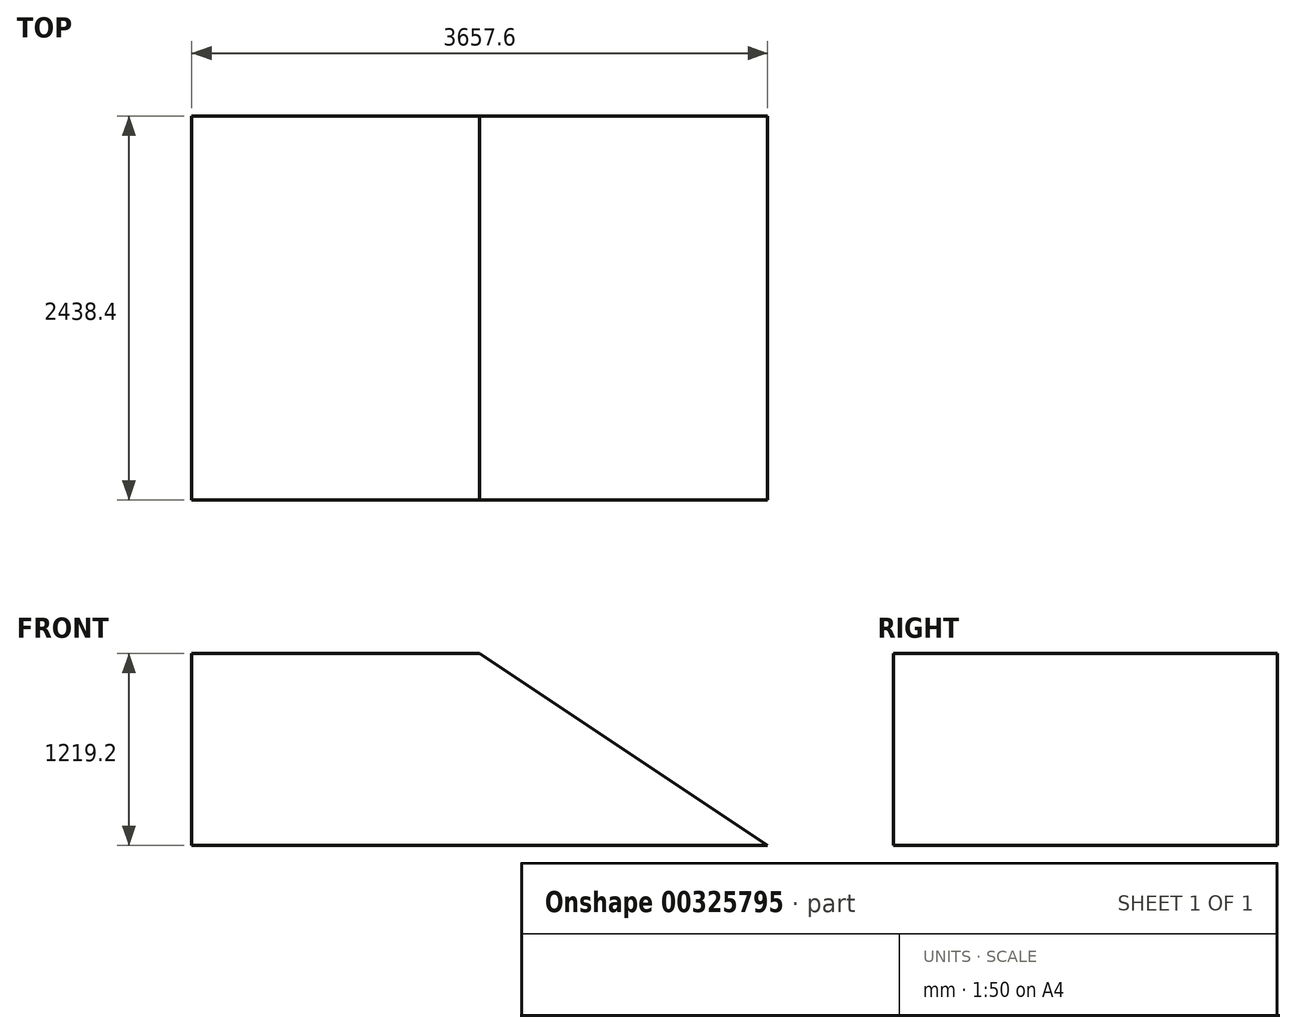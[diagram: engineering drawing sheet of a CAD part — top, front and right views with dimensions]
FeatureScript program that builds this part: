
annotation { "Feature Type Name" : "Feature", "Feature Type Description" : "" }
export const myFeature = defineFeature(function(context is Context, id is Id, definition is map)
    precondition{}
    {
        {
            var Q0;
            Q0=qCreatedBy(makeId("Front.planeOp"),FACE);
            var sketch = newSketch(context, id + "F0", { "sketchPlane" : qUnion([Q0])});
            skLineSegment(sketch, "E0.bottom", {"start": v(0, 0) * mm, "end": v(1828.8, 0) * mm});
            skLineSegment(sketch, "E0.top", {"start": v(0, 1219.2) * mm, "end": v(1828.8, 1219.2) * mm});
            skLineSegment(sketch, "E0.left", {"start": v(0, 0) * mm, "end": v(0, 1219.2) * mm});
            skLineSegment(sketch, "E0.right", {"start": v(1828.8, 0) * mm, "end": v(1828.8, 1219.2) * mm});
            skLineSegment(sketch, "E1", {"start": v(1828.8, 0) * mm, "end": v(3657.6, 0) * mm});
            skLineSegment(sketch, "E2", {"start": v(1828.8, 1219.2) * mm, "end": v(3657.6, 0) * mm});
            skSolve(sketch);
        }
        {
            var Q0;
            Q0=makeQuery(id+"F0.imprint","IMPRINT",FACE,{"disambiguationData":[TD([[makeQuery(id+"F0.imprint","IMPRINT",EDGE,{"derivedFrom":sQuery(id+"F0.wireOp",EDGE,"E0.left")}),1.0]])]});
            var Q1;
            Q1=makeQuery(id+"F0.imprint","IMPRINT",FACE,{"disambiguationData":[TD([[makeQuery(id+"F0.imprint","IMPRINT",EDGE,{"derivedFrom":sQuery(id+"F0.wireOp",EDGE,"E0.bottom")}),1.0]])]});
            var Q2;
            Q2=makeQuery(id+"F0.imprint","IMPRINT",FACE,{"disambiguationData":[TD([[makeQuery(id+"F0.imprint","IMPRINT",EDGE,{"derivedFrom":sQuery(id+"F0.wireOp",EDGE,"E0.right")}),-1.0]])]});
            var Q3;
            {var subQ0=sQuery(id+"F0.wireOp",EDGE,"XcISNvbV-igR6-hXD8-4gkA-qrv59Tn65qzj");Q3=makeQuery(id+"F0.imprint","IMPRINT",FACE,{"disambiguationData":[TD([[makeQuery(id+"F0.imprint","IMPRINT",EDGE,{"derivedFrom":subQ0}),-1.0]])]});}
            var Q4;
            {var subQ1=sQuery(id+"F0.wireOp",EDGE,"E0.top");var subQ3=sQuery(id+"F0.wireOp",EDGE,"B2NL7lis-7RjI-7pxC-DLYM-zCCmizm6cvdw");var subQ4=makeQuery(id+"F0.imprint","INTERSECT",VERTEX,{"derivedFrom":[subQ1,subQ3]});Q4=makeQuery(id+"F0.imprint","IMPRINT",FACE,{"disambiguationData":[TD([[makeQuery(id+"F0.imprint","IMPRINT",EDGE,{"disambiguationData":[TD([[subQ4,1.0]])],"derivedFrom":subQ3}),1.0]])]});}
            var Q5;
            {var subQ1=sQuery(id+"F0.wireOp",EDGE,"E0.top");var subQ3=sQuery(id+"F0.wireOp",EDGE,"B2NL7lis-7RjI-7pxC-DLYM-zCCmizm6cvdw");var subQ4=makeQuery(id+"F0.imprint","INTERSECT",VERTEX,{"derivedFrom":[subQ1,subQ3]});Q5=makeQuery(id+"F0.imprint","IMPRINT",FACE,{"disambiguationData":[TD([[makeQuery(id+"F0.imprint","IMPRINT",EDGE,{"disambiguationData":[TD([[subQ4,-1.0]])],"derivedFrom":subQ3}),1.0]])]});}
            extrude(context, id + "F1", {"entities" : qUnion([Q0, Q1, Q2, Q3, Q4, Q5]), "endBound" : BoundingType.SYMMETRIC, "oppositeDirection" : true, "depth" : 2438.4 * mm});
        }
    });
